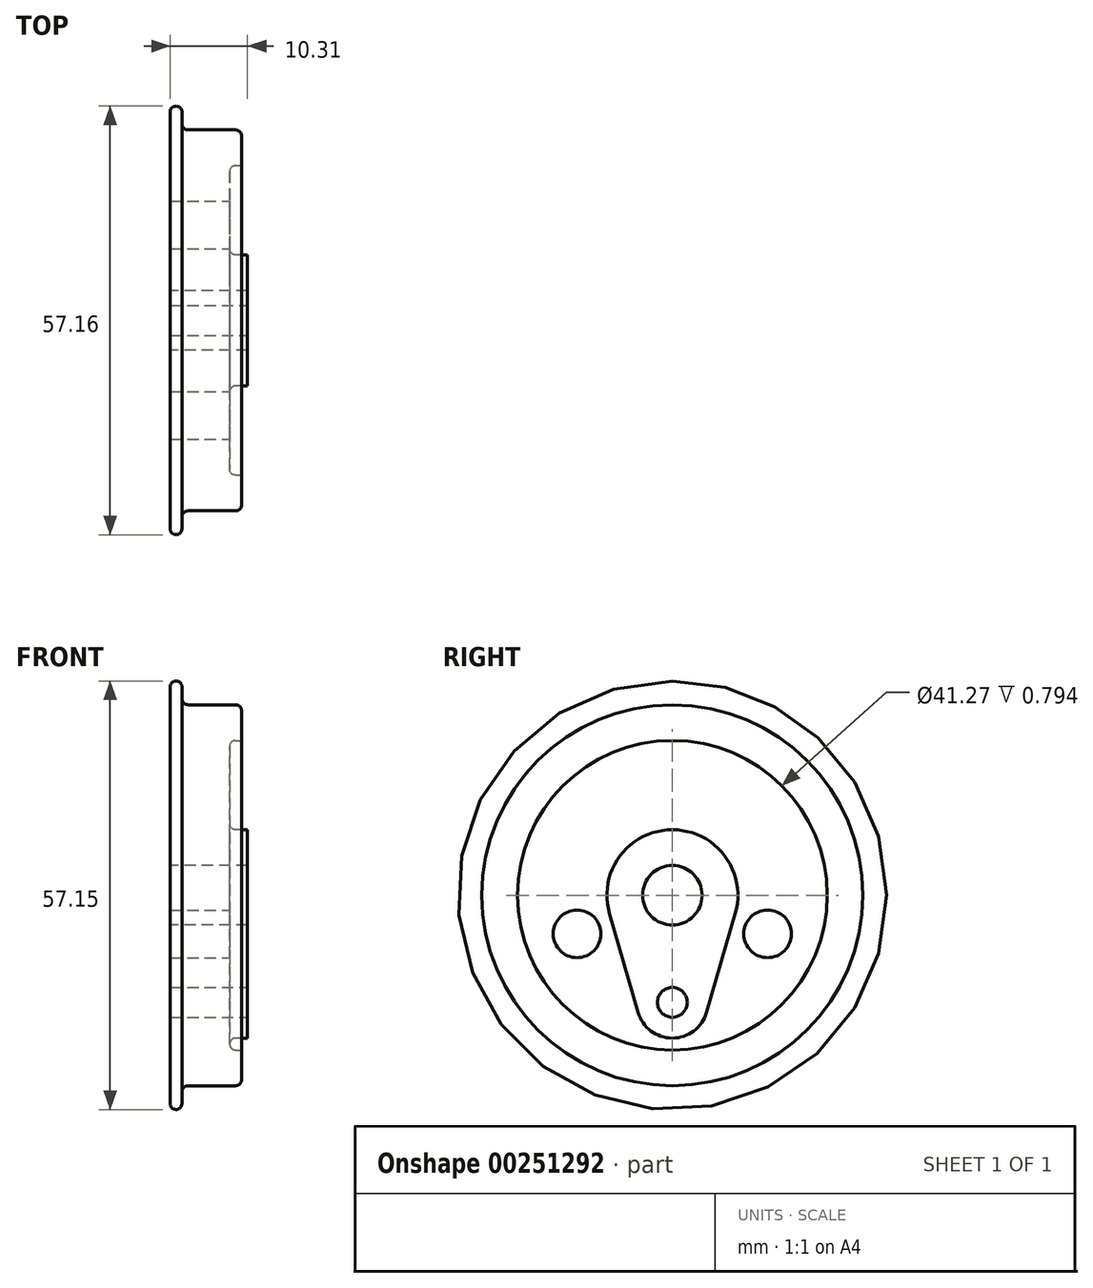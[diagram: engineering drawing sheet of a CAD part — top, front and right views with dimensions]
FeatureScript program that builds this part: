
annotation { "Feature Type Name" : "Feature", "Feature Type Description" : "" }
export const myFeature = defineFeature(function(context is Context, id is Id, definition is map)
    precondition{}
    {
        {
            var Q0;
            Q0=qCreatedBy(makeId("Front.planeOp"),FACE);
            var sketch = newSketch(context, id + "F0", { "sketchPlane" : qUnion([Q0])});
            skLineSegment(sketch, "E0", {"start": v(10.6, 36.32) * mm, "end": v(33.48, 36.32) * mm});
            skLineSegment(sketch, "E1", {"start": v(10.6, 36.32) * mm, "end": v(10.6, 8.53) * mm});
            skLineSegment(sketch, "E2", {"start": v(11.39, 7.74) * mm, "end": v(11.39, 7.74) * mm});
            skLineSegment(sketch, "E3", {"start": v(12.18, 8.53) * mm, "end": v(12.18, 10.12) * mm});
            skLineSegment(sketch, "E4", {"start": v(12.98, 10.92) * mm, "end": v(19.33, 10.92) * mm});
            skPoint(sketch, "E5.visualSharp", {"position": v(10.6, 7.74) * mm});
            skArc(sketch, "E5.filletArc", {"start": v(10.6, 8.53) * mm, "mid": v(10.83, 7.97) * mm, "end": v(11.39, 7.74) * mm});
            skPoint(sketch, "E6.visualSharp", {"position": v(12.18, 7.74) * mm});
            skArc(sketch, "E6.filletArc", {"start": v(11.39, 7.74) * mm, "mid": v(11.95, 7.97) * mm, "end": v(12.18, 8.53) * mm});
            skPoint(sketch, "E7.visualSharp", {"position": v(12.18, 10.92) * mm});
            skArc(sketch, "E7.filletArc", {"start": v(12.98, 10.92) * mm, "mid": v(12.42, 10.68) * mm, "end": v(12.18, 10.12) * mm});
            skLineSegment(sketch, "E8", {"start": v(20.12, 11.7) * mm, "end": v(20.12, 32.35) * mm});
            skLineSegment(sketch, "E9", {"start": v(20.12, 32.35) * mm, "end": v(10.6, 32.35) * mm});
            skPoint(sketch, "E10.visualSharp", {"position": v(20.12, 10.92) * mm});
            skArc(sketch, "E10.filletArc", {"start": v(19.33, 10.92) * mm, "mid": v(19.89, 11.15) * mm, "end": v(20.12, 11.7) * mm});
            skSolve(sketch);
        }
        {
            var Q0;
            Q0 = qSketchRegion(id + "F0", true);
            var Q1;
            Q1=sQuery(id+"F0.wireOp",EDGE,"E0");
            revolve(context, id + "F1", {"entities" : qUnion([Q0]), "axis" : qUnion([Q1]), "revolveType" : RevolveType.FULL});
        }
        {
            var Q0;
            Q0=makeQuery(id+"F1.opRevolve","SWEPT_FACE",FACE,{"disambiguationData":[OSD([sQuery(id+"F0.wireOp",EDGE,"E8")])]});
            var sketch = newSketch(context, id + "F2", { "sketchPlane" : qUnion([Q0])});
            skCircle(sketch, "E11", {"center": v(0, 36.32) * mm, "radius": 8.73 * mm});
            skCircle(sketch, "E12", {"center": v(0, 22.03) * mm, "radius": 1.98 * mm});
            skCircle(sketch, "E13", {"center": v(0, 22.03) * mm, "radius": 4.76 * mm});
            skCircle(sketch, "E14", {"center": v(0, 36.32) * mm, "radius": 19.05 * mm});
            skLineSegment(sketch, "E15", {"start": v(-8.39, 33.9) * mm, "end": v(-4.58, 20.7) * mm});
            skLineSegment(sketch, "E16", {"start": v(4.58, 20.7) * mm, "end": v(8.39, 33.9) * mm});
            skSolve(sketch);
        }
        {
            var Q0;
            Q0=makeQuery(id+"F2.imprint","IMPRINT",FACE,{"disambiguationData":[TD([[makeQuery(id+"F2.imprint","IMPRINT",EDGE,{"derivedFrom":sQuery(id+"F2.wireOp",EDGE,"E12")}),-1.0]])]});
            var Q1;
            {var subQ0=sQuery(id+"F2.wireOp",EDGE,"E15");Q1=makeQuery(id+"F2.imprint","IMPRINT",FACE,{"disambiguationData":[TD([[makeQuery(id+"F2.imprint","IMPRINT",EDGE,{"derivedFrom":subQ0}),1.0]])]});}
            var Q2;
            Q2=makeQuery(id+"F2.imprint","IMPRINT",FACE,{"disambiguationData":[TD([[makeQuery(id+"F2.imprint","IMPRINT",EDGE,{"derivedFrom":makeQuery(id+"F1.opRevolve","SWEPT_EDGE",EDGE,{"disambiguationData":[OSD([sQuery(id+"F0.wireOp",EDGE,"E8"),sQuery(id+"F0.wireOp",EDGE,"E9")])]})}),1.0]])]});
            var Q3;
            Q3=makeQuery(id+"F2.imprint","IMPRINT",FACE,{"disambiguationData":[TD([[makeQuery(id+"F2.imprint","IMPRINT",EDGE,{"derivedFrom":sQuery(id+"F2.wireOp",EDGE,"E12")}),1.0]])]});
            extrude(context, id + "F3", {"entities" : qUnion([Q0, Q1, Q2, Q3]), "operationType" : NewBodyOperationType.ADD, "depth" : 0.8 * mm});
        }
        {
            var Q0;
            Q0=makeQuery(id+"F3.opExtrude","CAP_FACE",FACE,{"disambiguationData":[OSD([sQuery(id+"F0.wireOp",EDGE,"E8"),sQuery(id+"F0.wireOp",EDGE,"E9"),sQuery(id+"F2.wireOp",EDGE,"E11"),sQuery(id+"F2.wireOp",EDGE,"E13"),sQuery(id+"F2.wireOp",EDGE,"E15"),sQuery(id+"F2.wireOp",EDGE,"E16")])],"isStart":false});
            var sketch = newSketch(context, id + "F4", { "sketchPlane" : qUnion([Q0])});
            skCircle(sketch, "E17", {"center": v(0, 22.03) * mm, "radius": 1.98 * mm});
            skSolve(sketch);
        }
        {
            var Q0;
            Q0=makeQuery(id+"F4.imprint","IMPRINT",FACE,{"disambiguationData":[TD([[makeQuery(id+"F4.imprint","IMPRINT",EDGE,{"derivedFrom":sQuery(id+"F4.wireOp",EDGE,"E17")}),1.0]])]});
            extrude(context, id + "F5", {"entities" : qUnion([Q0]), "operationType" : NewBodyOperationType.REMOVE, "oppositeDirection" : true, "depth" : 25.4 * mm});
        }
        {
            var Q0;
            Q0=makeQuery(id+"F1.opRevolve","SWEPT_FACE",FACE,{"disambiguationData":[OSD([sQuery(id+"F0.wireOp",EDGE,"E8")])]});
            var sketch = newSketch(context, id + "F6", { "sketchPlane" : qUnion([Q0])});
            skCircle(sketch, "E18", {"center": v(-12.7, 31.17) * mm, "radius": 3.18 * mm});
            skCircle(sketch, "E19", {"center": v(12.7, 31.17) * mm, "radius": 3.18 * mm});
            skSolve(sketch);
        }
        {
            var Q0;
            Q0 = qSketchRegion(id + "F6", true);
            extrude(context, id + "F7", {"entities" : qUnion([Q0]), "operationType" : NewBodyOperationType.REMOVE, "oppositeDirection" : true, "depth" : 25.4 * mm});
        }
        {
            var Q0;
            Q0=makeQuery(id+"F1.opRevolve","SWEPT_FACE",FACE,{"disambiguationData":[OSD([sQuery(id+"F0.wireOp",EDGE,"E8")])]});
            var sketch = newSketch(context, id + "F8", { "sketchPlane" : qUnion([Q0])});
            skCircle(sketch, "E20", {"center": v(0, 36.32) * mm, "radius": 20.64 * mm});
            skSolve(sketch);
        }
        {
            var Q0;
            Q0=makeQuery(id+"F8.imprint","IMPRINT",FACE,{"disambiguationData":[TD([[makeQuery(id+"F8.imprint","IMPRINT",EDGE,{"derivedFrom":sQuery(id+"F8.wireOp",EDGE,"E20")}),1.0]])]});
            extrude(context, id + "F9", {"entities" : qUnion([Q0]), "operationType" : NewBodyOperationType.REMOVE, "oppositeDirection" : true, "depth" : 1.59 * mm});
        }
        {
            var Q0;
            Q0=makeQuery(id+"F9.boolean.opBoolean","COPY",EDGE,{"derivedFrom":makeQuery(id+"F9.opExtrude","CAP_EDGE",EDGE,{"disambiguationData":[OSD([sQuery(id+"F8.wireOp",EDGE,"E20")])],"isStart":false})});
            var Q1;
            Q1=makeQuery(id+"F9.boolean.opBoolean","COPY",EDGE,{"derivedFrom":makeQuery(id+"F9.opExtrude","CAP_EDGE",EDGE,{"disambiguationData":[OSD([sQuery(id+"F2.wireOp",EDGE,"E16")])],"isStart":false})});
            fillet(context, id + "F10", {"entities" : qUnion([Q0, Q1]), "radius" : 0.8 * mm, "tangentPropagation" : true, "allowEdgeOverflow" : false});
        }
    });
